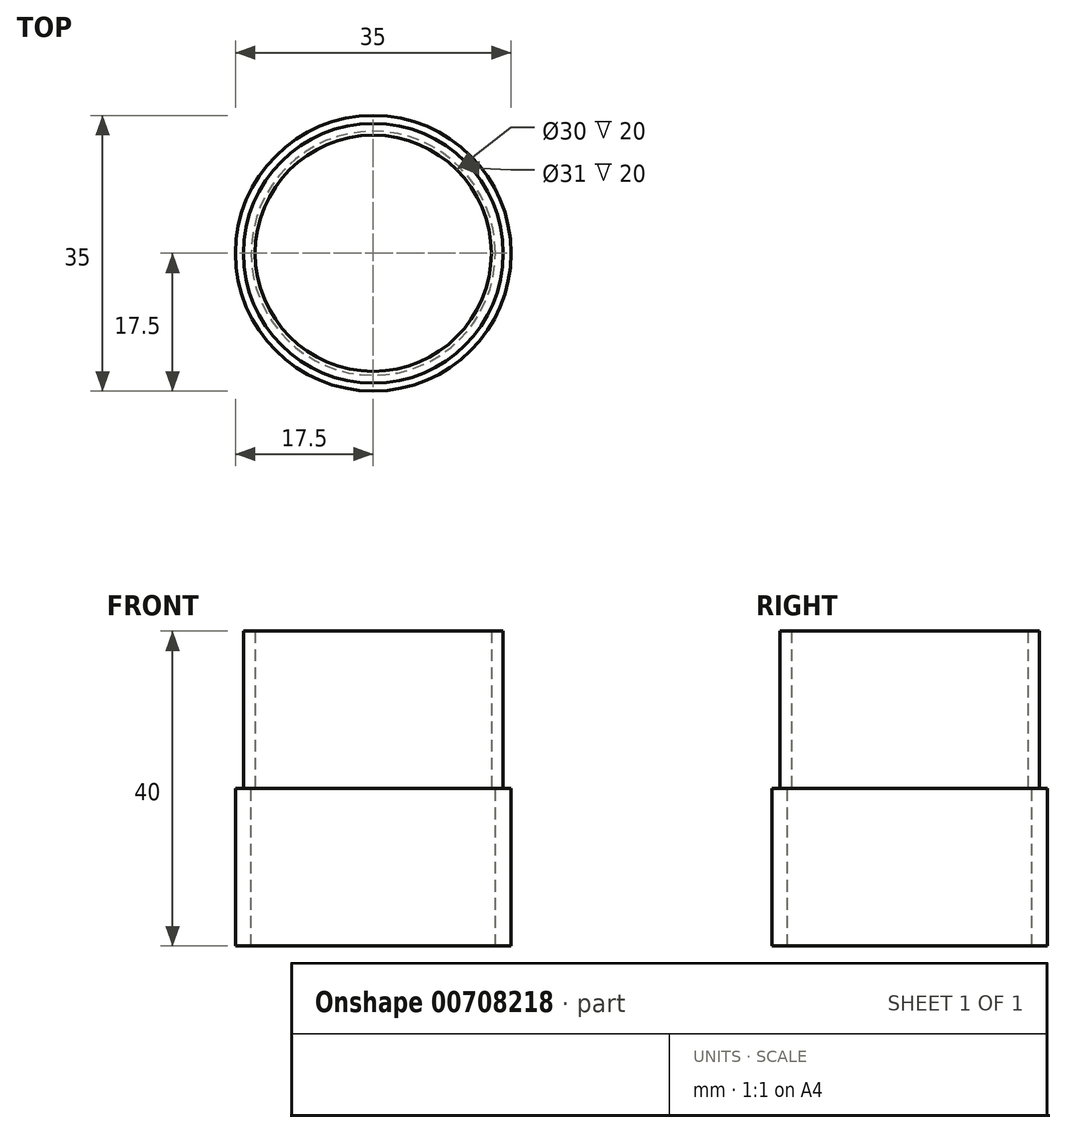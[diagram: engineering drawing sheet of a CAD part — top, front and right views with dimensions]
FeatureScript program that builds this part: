
annotation { "Feature Type Name" : "Feature", "Feature Type Description" : "" }
export const myFeature = defineFeature(function(context is Context, id is Id, definition is map)
    precondition{}
    {
        {
            var Q0;
            Q0=qCreatedBy(makeId("Top.planeOp"),FACE);
            var sketch = newSketch(context, id + "F0", { "sketchPlane" : qUnion([Q0])});
            skCircle(sketch, "E0", {"center": v(0, 0) * mm, "radius": 16.5 * mm});
            skCircle(sketch, "E1", {"center": v(0, 0) * mm, "radius": 15 * mm});
            skSolve(sketch);
        }
        {
            var Q0;
            Q0=makeQuery(id+"F0.imprint","IMPRINT",FACE,{"disambiguationData":[TD([[makeQuery(id+"F0.imprint","IMPRINT",EDGE,{"derivedFrom":sQuery(id+"F0.wireOp",EDGE,"E0")}),1.0]])]});
            extrude(context, id + "F1", {"entities" : qUnion([Q0]), "depth" : 20 * mm, "offsetDistance" : 25 * mm});
        }
        {
            var Q0;
            Q0=makeQuery(id+"F1.opExtrude","CAP_FACE",FACE,{"disambiguationData":[OSD([sQuery(id+"F0.wireOp",EDGE,"E0"),sQuery(id+"F0.wireOp",EDGE,"E1")])],"isStart":true});
            var sketch = newSketch(context, id + "F2", { "sketchPlane" : qUnion([Q0])});
            skCircle(sketch, "E2", {"center": v(0, 0) * mm, "radius": 17.5 * mm});
            skCircle(sketch, "E3", {"center": v(0, 0) * mm, "radius": 15.5 * mm});
            skSolve(sketch);
        }
        {
            var Q0;
            Q0 = qSketchRegion(id + "F2", true);
            extrude(context, id + "F3", {"entities" : qUnion([Q0]), "operationType" : NewBodyOperationType.ADD, "depth" : 20 * mm, "offsetDistance" : 25 * mm});
        }
    });
